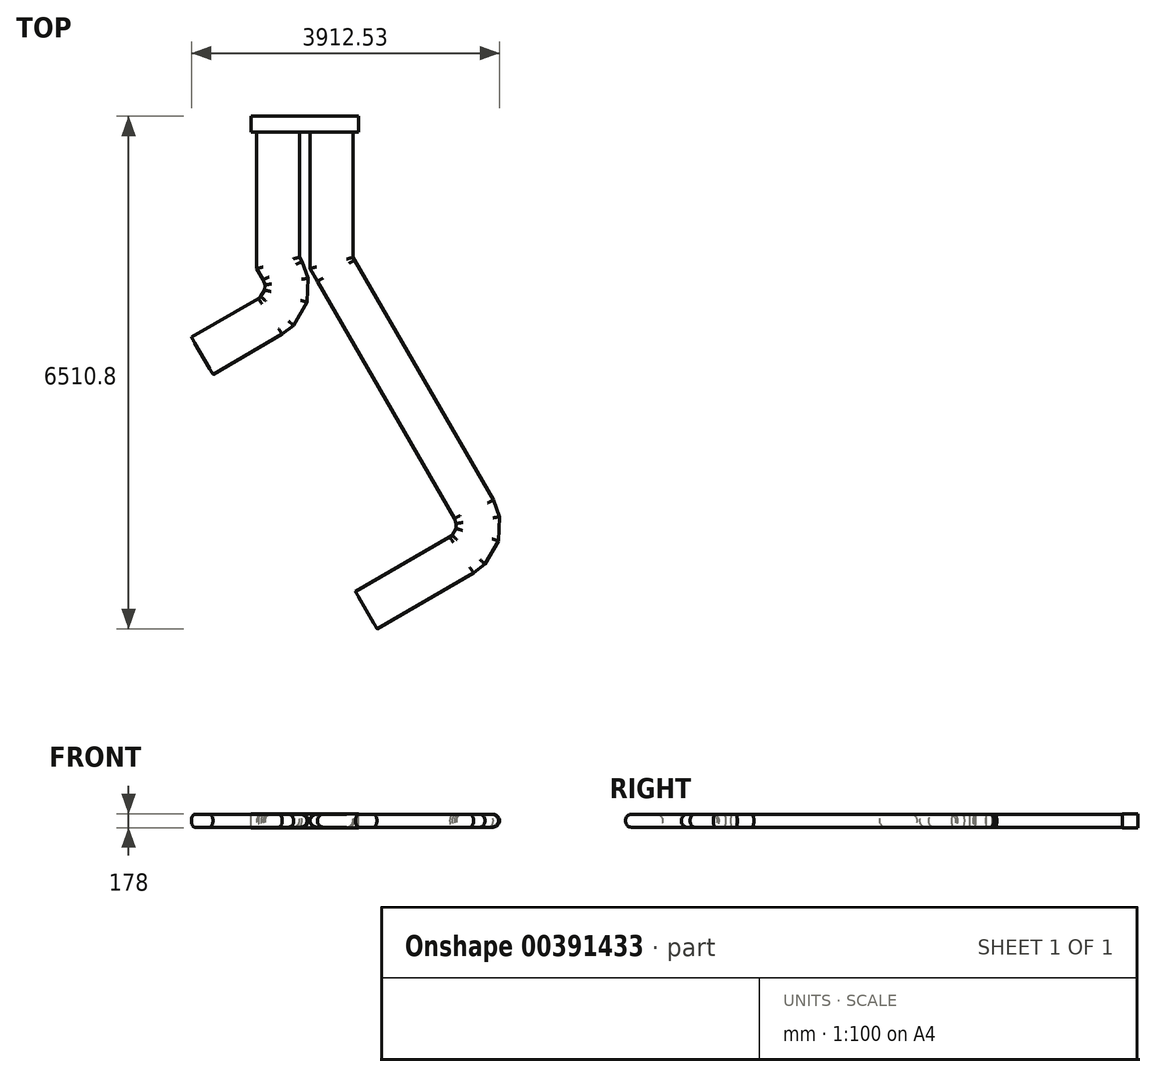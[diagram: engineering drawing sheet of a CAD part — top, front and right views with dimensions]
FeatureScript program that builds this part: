
annotation { "Feature Type Name" : "Feature", "Feature Type Description" : "" }
export const myFeature = defineFeature(function(context is Context, id is Id, definition is map)
    precondition{}
    {
        {
            var Q0;
            Q0=qCreatedBy(makeId("Front.planeOp"),FACE);
            var sketch = newSketch(context, id + "F0", { "sketchPlane" : qUnion([Q0])});
            skLineSegment(sketch, "E0.bottom", {"start": v(680, -89) * mm, "end": v(-680, -89) * mm});
            skLineSegment(sketch, "E0.top", {"start": v(680, 89) * mm, "end": v(-680, 89) * mm});
            skLineSegment(sketch, "E0.left", {"start": v(680, -89) * mm, "end": v(680, 89) * mm});
            skLineSegment(sketch, "E0.right", {"start": v(-680, -89) * mm, "end": v(-680, 89) * mm});
            skPoint(sketch, "E0.middle", {"position": v(0, 0) * mm});
            skSolve(sketch);
        }
        {
            var Q0;
            Q0=qSketchRegion(id+"F0",true);
            extrude(context, id + "F1", {"entities" : qUnion([Q0]), "depth" : 200 * mm});
        }
        {
            var Q0;
            Q0=makeQuery(id+"F1.opExtrude","CAP_FACE",FACE,{"disambiguationData":[OSD([sQuery(id+"F0.wireOp",EDGE,"E0.bottom"),sQuery(id+"F0.wireOp",EDGE,"E0.top"),sQuery(id+"F0.wireOp",EDGE,"E0.left"),sQuery(id+"F0.wireOp",EDGE,"E0.right")])],"isStart":false});
            var sketch = newSketch(context, id + "F2", { "sketchPlane" : qUnion([Q0])});
            skLineSegment(sketch, "E1.bottom", {"start": v(-150, -82.5) * mm, "end": v(-530, -82.5) * mm});
            skLineSegment(sketch, "E1.top", {"start": v(-150, 82.5) * mm, "end": v(-530, 82.5) * mm});
            skPoint(sketch, "E1.middle", {"position": v(-340, 0) * mm});
            skArc(sketch, "E2", {"start": v(-530, 82.5) * mm, "mid": v(-612.5, 0) * mm, "end": v(-530, -82.5) * mm});
            skArc(sketch, "E3", {"start": v(-150, -82.5) * mm, "mid": v(-67.5, 0) * mm, "end": v(-150, 82.5) * mm});
            skLineSegment(sketch, "E4.MirrorCS", {"start": v(150, -82.5) * mm, "end": v(530, -82.5) * mm});
            skLineSegment(sketch, "E5.MirrorCS", {"start": v(150, 82.5) * mm, "end": v(530, 82.5) * mm});
            skArc(sketch, "E6.MirrorCS", {"start": v(150, -82.5) * mm, "mid": v(67.5, 0) * mm, "end": v(150, 82.5) * mm});
            skArc(sketch, "E7.MirrorCS", {"start": v(530, 82.5) * mm, "mid": v(612.5, 0) * mm, "end": v(530, -82.5) * mm});
            skSolve(sketch);
        }
        {
            var Q0;
            Q0=makeQuery(id+"F2.imprint","IMPRINT",FACE,{"disambiguationData":[TD([[makeQuery(id+"F2.imprint","IMPRINT",EDGE,{"derivedFrom":sQuery(id+"F2.wireOp",EDGE,"E1.bottom")}),-1.0]])]});
            var Q1;
            Q1=makeQuery(id+"F2.imprint","IMPRINT",FACE,{"disambiguationData":[TD([[makeQuery(id+"F2.imprint","IMPRINT",EDGE,{"derivedFrom":sQuery(id+"F2.wireOp",EDGE,"E4.MirrorCS")}),1.0]])]});
            extrude(context, id + "F3", {"entities" : qUnion([Q0, Q1]), "operationType" : NewBodyOperationType.ADD, "depth" : 50 * mm});
        }
        {
            var Q0;
            Q0=makeQuery(id+"F1.opExtrude","SWEPT_BODY",BODY,{"disambiguationData":[OSD([sQuery(id+"F0.wireOp",EDGE,"E0.bottom"),sQuery(id+"F0.wireOp",EDGE,"E0.top"),sQuery(id+"F0.wireOp",EDGE,"E0.left"),sQuery(id+"F0.wireOp",EDGE,"E0.right")])]});
            transform(context, id + "F4", {"entities" : qUnion([Q0]), "transformType" : TransformType.TRANSLATION_3D, "dx" : 0 * mm, "dy" : 0 * mm, "dz" : 0 * mm, "makeCopy" : true});
        }
        {
            var Q0;
            Q0=makeQuery(id+"F4.opPattern","COPY",BODY,{"derivedFrom":makeQuery(id+"F1.opExtrude","SWEPT_BODY",BODY,{"disambiguationData":[OSD([sQuery(id+"F0.wireOp",EDGE,"E0.bottom"),sQuery(id+"F0.wireOp",EDGE,"E0.top"),sQuery(id+"F0.wireOp",EDGE,"E0.left"),sQuery(id+"F0.wireOp",EDGE,"E0.right")])]}),"instanceName":"1"});
            deleteBodies(context, id + "F5", {"entities" : qUnion([Q0])});
        }
        {
            var Q0;
            Q0=makeQuery(id+"F1.opExtrude","SWEPT_BODY",BODY,{"disambiguationData":[OSD([sQuery(id+"F0.wireOp",EDGE,"E0.bottom"),sQuery(id+"F0.wireOp",EDGE,"E0.top"),sQuery(id+"F0.wireOp",EDGE,"E0.left"),sQuery(id+"F0.wireOp",EDGE,"E0.right")])]});
            transform(context, id + "F6", {"entities" : qUnion([Q0]), "transformType" : TransformType.COPY});
        }
        {
            var Q0;
            Q0=makeQuery(id+"F6.opPattern","COPY",BODY,{"derivedFrom":makeQuery(id+"F1.opExtrude","SWEPT_BODY",BODY,{"disambiguationData":[OSD([sQuery(id+"F0.wireOp",EDGE,"E0.bottom"),sQuery(id+"F0.wireOp",EDGE,"E0.top"),sQuery(id+"F0.wireOp",EDGE,"E0.left"),sQuery(id+"F0.wireOp",EDGE,"E0.right")])]}),"instanceName":"1"});
            transform(context, id + "F7", {"entities" : qUnion([Q0]), "transformType" : TransformType.TRANSLATION_3D, "dx" : 0 * mm, "dy" : 0 * mm, "dz" : 0 * mm, "makeCopy" : true});
        }
        {
            var Q0;
            Q0=makeQuery(id+"F7.opPattern","COPY",BODY,{"derivedFrom":makeQuery(id+"F6.opPattern","COPY",BODY,{"derivedFrom":makeQuery(id+"F1.opExtrude","SWEPT_BODY",BODY,{"disambiguationData":[OSD([sQuery(id+"F0.wireOp",EDGE,"E0.bottom"),sQuery(id+"F0.wireOp",EDGE,"E0.top"),sQuery(id+"F0.wireOp",EDGE,"E0.left"),sQuery(id+"F0.wireOp",EDGE,"E0.right")])]}),"instanceName":"1"}),"instanceName":"1"});
            deleteBodies(context, id + "F8", {"entities" : qUnion([Q0])});
        }
        {
            var Q0;
            Q0=makeQuery(id+"F6.opPattern","COPY",BODY,{"derivedFrom":makeQuery(id+"F1.opExtrude","SWEPT_BODY",BODY,{"disambiguationData":[OSD([sQuery(id+"F0.wireOp",EDGE,"E0.bottom"),sQuery(id+"F0.wireOp",EDGE,"E0.top"),sQuery(id+"F0.wireOp",EDGE,"E0.left"),sQuery(id+"F0.wireOp",EDGE,"E0.right")])]}),"instanceName":"1"});
            deleteBodies(context, id + "F9", {"entities" : qUnion([Q0])});
        }
        {
            var Q0;
            Q0=makeQuery(id+"F3.opExtrude","CAP_FACE",FACE,{"disambiguationData":[OSD([sQuery(id+"F2.wireOp",EDGE,"E1.bottom"),sQuery(id+"F2.wireOp",EDGE,"E1.top"),sQuery(id+"F2.wireOp",EDGE,"E2"),sQuery(id+"F2.wireOp",EDGE,"E3")])],"isStart":false});
            var sketch = newSketch(context, id + "F10", { "sketchPlane" : qUnion([Q0])});
            skSolve(sketch);
        }
        {
            var Q0;
            Q0=makeQuery(id+"F10.imprint","IMPRINT",FACE,{"disambiguationData":[TD([[makeQuery(id+"F10.imprint","IMPRINT",EDGE,{"derivedFrom":makeQuery(id+"F3.opExtrude","CAP_EDGE",EDGE,{"disambiguationData":[OSD([sQuery(id+"F2.wireOp",EDGE,"E1.bottom")])],"isStart":false})}),-1.0]])]});
            var sketch = newSketch(context, id + "F11", { "sketchPlane" : qUnion([Q0])});
            skPoint(sketch, "E8.0", {"position": v(-340, 82.5) * mm});
            skPoint(sketch, "E8.1", {"position": v(-340, -82.5) * mm});
            skPoint(sketch, "E8.2", {"position": v(-612.5, 0) * mm});
            skPoint(sketch, "E8.3", {"position": v(-67.5, 0) * mm});
            skPoint(sketch, "E8.4", {"position": v(67.5, 0) * mm});
            skPoint(sketch, "E8.5", {"position": v(340, -82.5) * mm});
            skPoint(sketch, "E8.6", {"position": v(340, 82.5) * mm});
            skPoint(sketch, "E8.7", {"position": v(612.5, 0) * mm});
            skLineSegment(sketch, "E9", {"start": v(-612.5, 0) * mm, "end": v(612.5, 0) * mm, "construction": true});
            skLineSegment(sketch, "E10", {"start": v(-340, 82.5) * mm, "end": v(-340, -82.5) * mm, "construction": true});
            skLineSegment(sketch, "E11", {"start": v(340, 82.5) * mm, "end": v(340, -82.5) * mm, "construction": true});
            skPoint(sketch, "E12", {"position": v(-340, 0) * mm});
            skPoint(sketch, "E13", {"position": v(340, 0) * mm});
            skSolve(sketch);
        }
        {
            var Q0;
            Q0=qCreatedBy(makeId("Top.planeOp"),FACE);
            var sketch = newSketch(context, id + "F12", { "sketchPlane" : qUnion([Q0])});
            skPoint(sketch, "E14.0", {"position": v(340, -250) * mm});
            skPoint(sketch, "E14.1", {"position": v(-340, -250) * mm});
            skLineSegment(sketch, "E15", {"start": v(-340, -250) * mm, "end": v(-340, -1750) * mm});
            skLineSegment(sketch, "E16", {"start": v(340, -250) * mm, "end": v(340, -1750) * mm});
            skLineSegment(sketch, "E17", {"start": v(-283.06, -1962.5) * mm, "end": v(85, -1750) * mm, "construction": true});
            skLineSegment(sketch, "E18", {"start": v(395.32, -1963.44) * mm, "end": v(763.27, -1750.74) * mm, "construction": true});
            skLineSegment(sketch, "E19", {"start": v(-340, -1750) * mm, "end": v(85, -1750) * mm, "construction": true});
            skLineSegment(sketch, "E20", {"start": v(340, -1750) * mm, "end": v(765, -1750) * mm, "construction": true});
            skLineSegment(sketch, "E21", {"start": v(-340, -1750) * mm, "end": v(-340, -1864) * mm});
            skLineSegment(sketch, "E22", {"start": v(340, -1750) * mm, "end": v(340, -1864) * mm});
            skLineSegment(sketch, "E23", {"start": v(-340, -1864) * mm, "end": v(-283.06, -1962.5) * mm});
            skLineSegment(sketch, "E24", {"start": v(340, -1864) * mm, "end": v(395.32, -1963.44) * mm});
            skLineSegment(sketch, "E25", {"start": v(-283.06, -1962.5) * mm, "end": v(-651, -2175.2) * mm, "construction": true});
            skLineSegment(sketch, "E26", {"start": v(-651, -2175.2) * mm, "end": v(-232.5, -2101.17) * mm, "construction": true});
            skPoint(sketch, "E27", {"position": v(-438.31, -2543.14) * mm});
            skPoint(sketch, "E28", {"position": v(-350.33, -2475.56) * mm});
            skPoint(sketch, "E29", {"position": v(-240.43, -2284.98) * mm});
            skPoint(sketch, "E30", {"position": v(-232.5, -2101.17) * mm});
            skLineSegment(sketch, "E31", {"start": v(-283.06, -1962.5) * mm, "end": v(-232.5, -2101.17) * mm});
            skLineSegment(sketch, "E32", {"start": v(-232.5, -2101.17) * mm, "end": v(-240.43, -2284.98) * mm});
            skLineSegment(sketch, "E33", {"start": v(-240.43, -2284.98) * mm, "end": v(-350.33, -2475.56) * mm});
            skLineSegment(sketch, "E34", {"start": v(-350.33, -2475.56) * mm, "end": v(-438.31, -2543.14) * mm});
            skLineSegment(sketch, "E35", {"start": v(-438.31, -2543.14) * mm, "end": v(-651, -2175.2) * mm, "construction": true});
            skLineSegment(sketch, "E36", {"start": v(-438.31, -2543.14) * mm, "end": v(-1304.07, -3043.6) * mm});
            skLineSegment(sketch, "E37", {"start": v(395.32, -1963.44) * mm, "end": v(2146.94, -4993.59) * mm});
            skLineSegment(sketch, "E38", {"start": v(2146.94, -4993.59) * mm, "end": v(1779, -5206.29) * mm, "construction": true});
            skLineSegment(sketch, "E39", {"start": v(1779, -5206.29) * mm, "end": v(2197.5, -5132.26) * mm, "construction": true});
            skPoint(sketch, "E40", {"position": v(1991.69, -5574.23) * mm});
            skPoint(sketch, "E41", {"position": v(2079.67, -5506.64) * mm});
            skPoint(sketch, "E42", {"position": v(2189.57, -5316.06) * mm});
            skPoint(sketch, "E43", {"position": v(2197.5, -5132.26) * mm});
            skLineSegment(sketch, "E44", {"start": v(2146.94, -4993.59) * mm, "end": v(2197.5, -5132.26) * mm});
            skLineSegment(sketch, "E45", {"start": v(2197.5, -5132.26) * mm, "end": v(2189.57, -5316.06) * mm});
            skLineSegment(sketch, "E46", {"start": v(2189.57, -5316.06) * mm, "end": v(2079.67, -5506.64) * mm});
            skLineSegment(sketch, "E47", {"start": v(2079.67, -5506.64) * mm, "end": v(1991.69, -5574.23) * mm});
            skLineSegment(sketch, "E48", {"start": v(1779, -5206.29) * mm, "end": v(1991.69, -5574.23) * mm, "construction": true});
            skLineSegment(sketch, "E49", {"start": v(1991.69, -5574.23) * mm, "end": v(779.63, -6274.88) * mm});
            skSolve(sketch);
        }
        {
            var Q0;
            Q0=makeQuery(id+"F11.imprint","IMPRINT",FACE,{"disambiguationData":[TD([[makeQuery(id+"F11.imprint","IMPRINT",EDGE,{"derivedFrom":makeQuery(id+"F10.imprint","IMPRINT",EDGE,{"derivedFrom":makeQuery(id+"F3.opExtrude","CAP_EDGE",EDGE,{"disambiguationData":[OSD([sQuery(id+"F2.wireOp",EDGE,"E1.bottom")])],"isStart":false})})}),-1.0]])]});
            var Q1;
            Q1=sQuery(id+"F12.wireOp",EDGE,"E15");
            var Q2;
            Q2=sQuery(id+"F12.wireOp",EDGE,"E21");
            var Q3;
            Q3=sQuery(id+"F12.wireOp",EDGE,"E23");
            var Q4;
            Q4=sQuery(id+"F12.wireOp",EDGE,"E31");
            var Q5;
            Q5=sQuery(id+"F12.wireOp",EDGE,"E32");
            var Q6;
            Q6=sQuery(id+"F12.wireOp",EDGE,"E33");
            var Q7;
            Q7=sQuery(id+"F12.wireOp",EDGE,"E34");
            var Q8;
            Q8=sQuery(id+"F12.wireOp",EDGE,"E36");
            sweep(context, id + "F13", {"operationType" : NewBodyOperationType.ADD, "profiles" : qUnion([Q0]), "path" : qUnion([Q1, Q2, Q3, Q4, Q5, Q6, Q7, Q8])});
        }
        {
            var Q0;
            Q0=makeQuery(id+"F3.opExtrude","CAP_FACE",FACE,{"disambiguationData":[OSD([sQuery(id+"F2.wireOp",EDGE,"E4.MirrorCS"),sQuery(id+"F2.wireOp",EDGE,"E5.MirrorCS"),sQuery(id+"F2.wireOp",EDGE,"E6.MirrorCS"),sQuery(id+"F2.wireOp",EDGE,"E7.MirrorCS")])],"isStart":false});
            var Q1;
            Q1=sQuery(id+"F12.wireOp",EDGE,"E16");
            var Q2;
            Q2=sQuery(id+"F12.wireOp",EDGE,"E22");
            var Q3;
            Q3=sQuery(id+"F12.wireOp",EDGE,"E24");
            var Q4;
            Q4=sQuery(id+"F12.wireOp",EDGE,"E37");
            var Q5;
            Q5=sQuery(id+"F12.wireOp",EDGE,"E44");
            var Q6;
            Q6=sQuery(id+"F12.wireOp",EDGE,"E45");
            var Q7;
            Q7=sQuery(id+"F12.wireOp",EDGE,"E46");
            var Q8;
            Q8=sQuery(id+"F12.wireOp",EDGE,"E47");
            var Q9;
            Q9=sQuery(id+"F12.wireOp",EDGE,"E49");
            sweep(context, id + "F14", {"operationType" : NewBodyOperationType.ADD, "profiles" : qUnion([Q0]), "path" : qUnion([Q1, Q2, Q3, Q4, Q5, Q6, Q7, Q8, Q9])});
        }
        {
            var Q0;
            Q0=makeQuery(id+"F13.opSweep","CAP_FACE",FACE,{"disambiguationData":[OSD([sQuery(id+"F2.wireOp",EDGE,"E1.bottom"),sQuery(id+"F2.wireOp",EDGE,"E1.top"),sQuery(id+"F2.wireOp",EDGE,"E2"),sQuery(id+"F2.wireOp",EDGE,"E3"),sQuery(id+"F12.wireOp",VERTEX,"E36.end")])],"isStart":false});
            var sketch = newSketch(context, id + "F15", { "sketchPlane" : qUnion([Q0])});
            skLineSegment(sketch, "E50", {"start": v(2254.89, 0) * mm, "end": v(1709.89, 0) * mm, "construction": true});
            skLineSegment(sketch, "E51", {"start": v(1982.39, 82.5) * mm, "end": v(1982.39, -82.5) * mm, "construction": true});
            skSolve(sketch);
        }
        {
            var Q0;
            Q0=sQuery(id+"F15.wireOp",EDGE,"E50");
            cPlane(context, id + "F16", {"entities" : qUnion([Q0]), "cplaneType" : CPlaneType.LINE_ANGLE, "offset" : 25 * mm, "angle" : 0 * degree, "width" : 150 * mm, "height" : 150 * mm});
        }
    });
